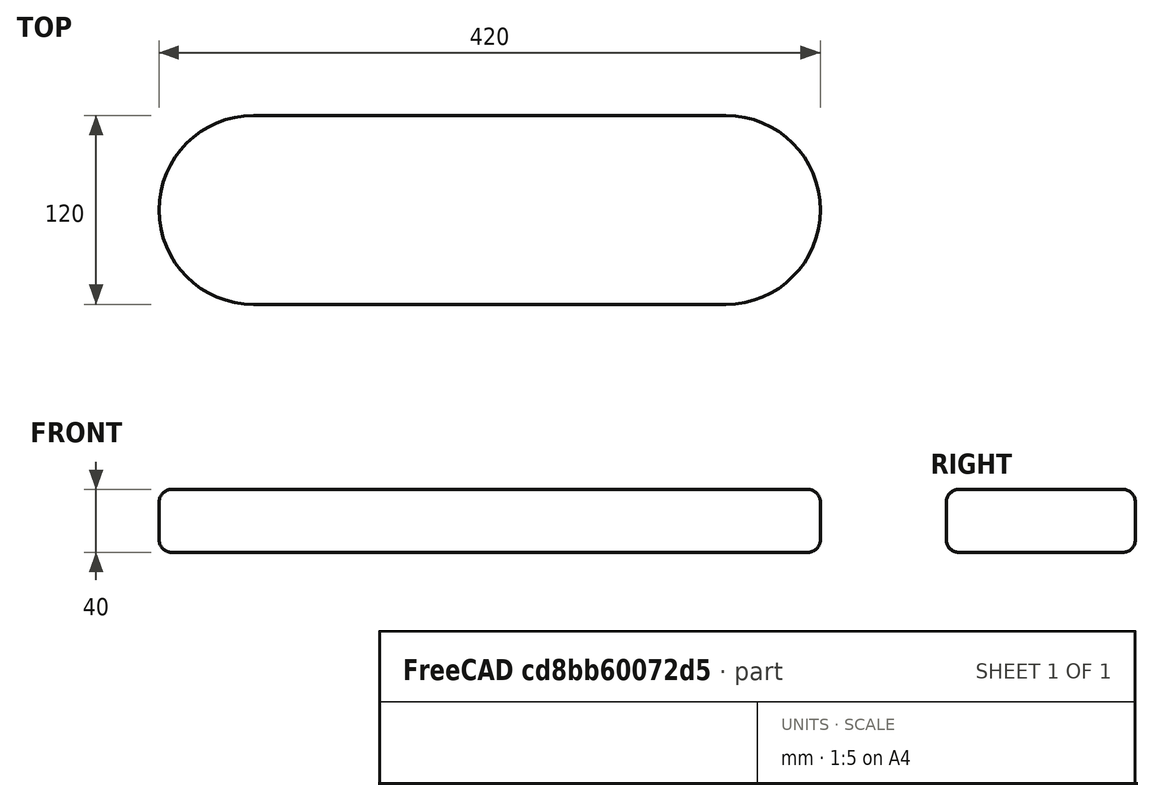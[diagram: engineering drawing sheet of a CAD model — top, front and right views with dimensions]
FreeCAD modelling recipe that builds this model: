
FCSTD DOCUMENT  (FreeCAD 0.20R29410 (Git))
Label: lk1
License: All rights reserved
LicenseURL: http://en.wikipedia.org/wiki/All_rights_reserved
objects: Sketcher::SketchObject×1, PartDesign::Pad×1, PartDesign::Fillet×1, PartDesign::Body×1, Mesh::Feature×1
note: 6 computed .brp shape members not serialized (recipe doc carries the construction recipe); baked Part::Feature solids carry a one-line shape summary decoded from their .brp

FEATURE [Sketcher::SketchObject] Sketch
  FullyConstrained = true
  MapMode = 5
  Support = -> [XY_Plane]
  sketch-geometry (4):
    g0: LineSegment StartX=-0.000106924 StartY=60 StartZ=0 EndX=300 EndY=60 EndZ=0
    g1: LineSegment StartX=300 StartY=-60 StartZ=0 EndX=-0.000106924 EndY=-60 EndZ=0
    g2: ArcOfCircle CenterX=0 CenterY=0 CenterZ=0 NormalX=0 NormalY=0 NormalZ=1 AngleXU=0 Radius=60 StartAngle=1.5708 EndAngle=4.71239
    g3: ArcOfCircle CenterX=300 CenterY=0 CenterZ=0 NormalX=0 NormalY=0 NormalZ=1 AngleXU=0 Radius=60 StartAngle=4.71239 EndAngle=7.85398
  constraints (13):
    c: Horizontal(g0)
    c: Horizontal(g1)
    c: Coincident(g2,g0)
    c: Coincident(g2,g1)
    c: Coincident(g3,g1)
    c: Coincident(g3,g0)
    c: DistanceX(g2,g3) = 300
    c: Equal(g2,g3)
    c: PointOnObject(g3,g-1)
    c: Vertical(g3,g0)
    c: Diameter(g3) = 120
    c: Vertical(g1,g0)
    c: Coincident(g-1,g2)
FEATURE [PartDesign::Pad] Pad
  Direction = (1,1,1)
  Length = 40
  Length2 = 100
  Profile = -> Sketch
  Type = 0
FEATURE [PartDesign::Fillet] Fillet
  Base = -> Pad [Face6,Face5]
  BaseFeature = -> Pad
  Radius = 8
  SupportTransform = false
  UseAllEdges = false
FEATURE [PartDesign::Body] Body
  Group = -> [Sketch,Pad,Fillet]
  Origin = -> Origin
  Tip = -> Fillet
FEATURE [Mesh::Feature] Mesh  label="Body (Meshed)"
